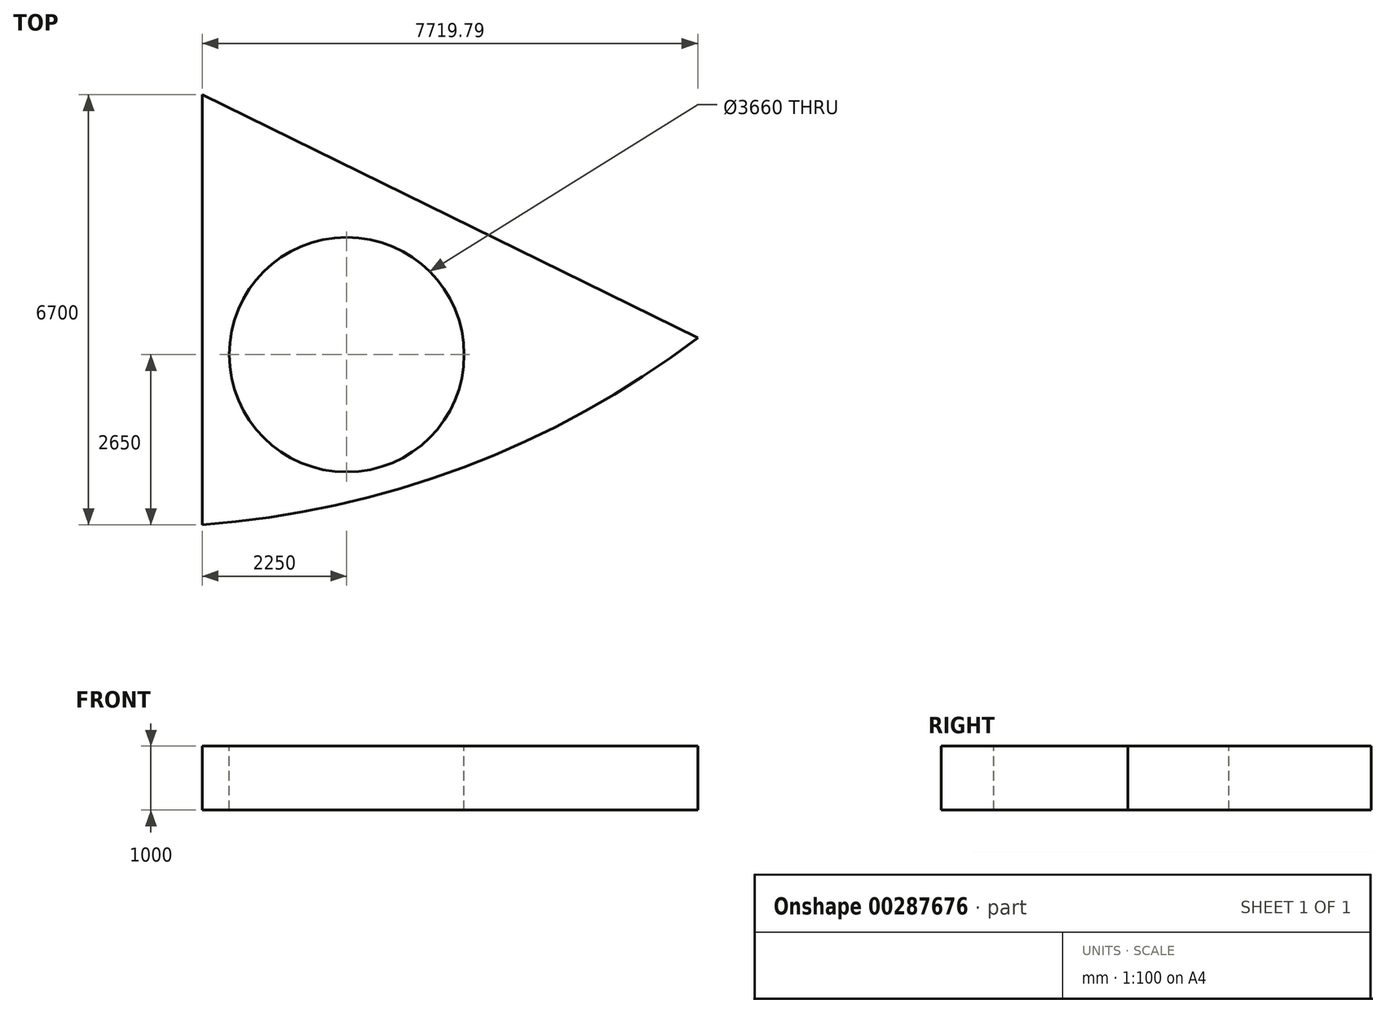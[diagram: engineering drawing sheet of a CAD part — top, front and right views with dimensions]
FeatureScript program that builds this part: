
annotation { "Feature Type Name" : "Feature", "Feature Type Description" : "" }
export const myFeature = defineFeature(function(context is Context, id is Id, definition is map)
    precondition{}
    {
        {
            var Q0;
            Q0=qCreatedBy(makeId("Top.planeOp"),FACE);
            var sketch = newSketch(context, id + "F0", { "sketchPlane" : qUnion([Q0])});
            skLineSegment(sketch, "E0", {"start": v(-42.55, -996.44) * mm, "end": v(-42.55, 5703.56) * mm});
            skPoint(sketch, "E1.start.orphan", {"position": v(1957.45, -996.44) * mm});
            skLineSegment(sketch, "E2", {"start": v(-42.55, 5703.56) * mm, "end": v(7677.24, 1913.44) * mm});
            skLineSegment(sketch, "E3", {"start": v(7677.24, 1913.44) * mm, "end": v(-42.55, -996.44) * mm, "construction": true});
            skLineSegment(sketch, "E4", {"start": v(3817.34, 458.5) * mm, "end": v(4028.97, -102.94) * mm, "construction": true});
            skArc(sketch, "E5", {"start": v(-42.55, -996.44) * mm, "mid": v(4028.97, -102.94) * mm, "end": v(7677.24, 1913.44) * mm});
            skCircle(sketch, "E6", {"center": v(2207.45, 1653.56) * mm, "radius": 1830 * mm});
            skSolve(sketch);
        }
        {
            var Q0;
            Q0 = qSketchRegion(id + "F0", true);
            extrude(context, id + "F1", {"entities" : qUnion([Q0]), "oppositeDirection" : true, "depth" : 1000 * mm});
        }
    });
